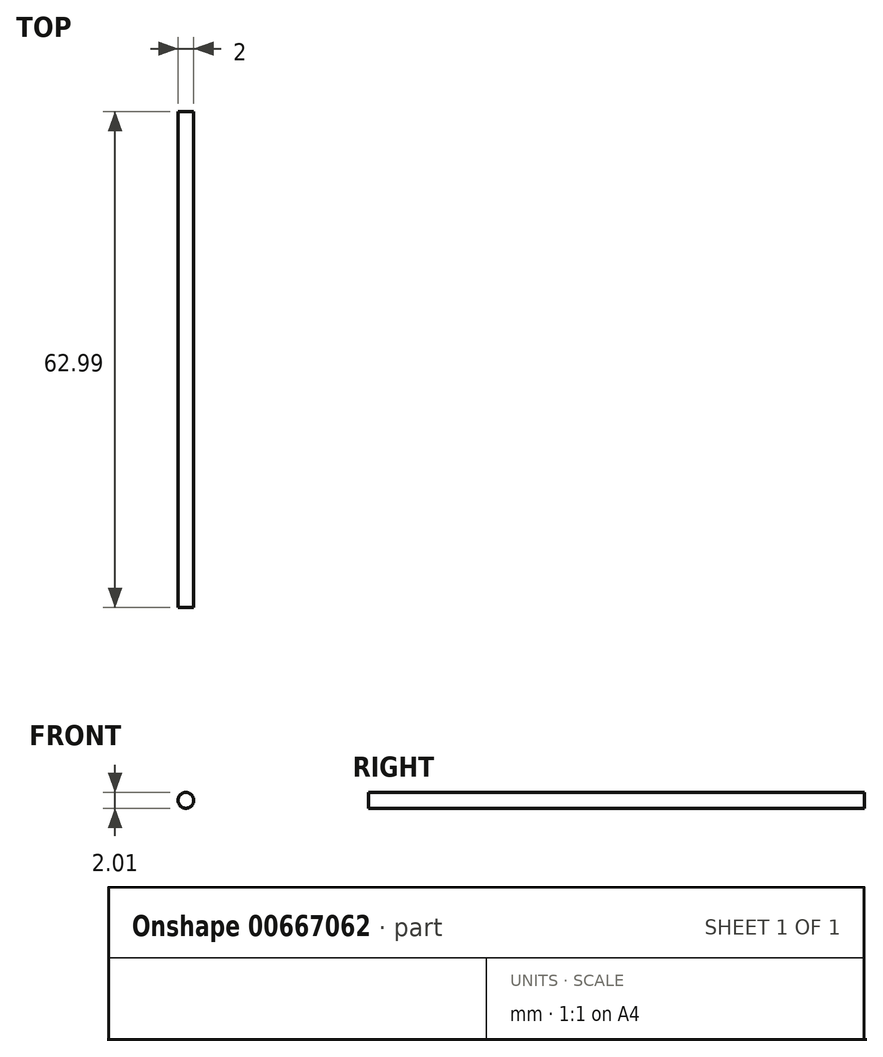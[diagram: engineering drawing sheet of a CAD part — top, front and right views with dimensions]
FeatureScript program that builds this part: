
annotation { "Feature Type Name" : "Feature", "Feature Type Description" : "" }
export const myFeature = defineFeature(function(context is Context, id is Id, definition is map)
    precondition{}
    {
        {
            var Q0;
            Q0=qCreatedBy(makeId("Front.planeOp"),FACE);
            var sketch = newSketch(context, id + "F0", { "sketchPlane" : qUnion([Q0])});
            skCircle(sketch, "E0", {"center": v(-42.49, 34.9) * mm, "radius": 1 * mm});
            skSolve(sketch);
        }
        {
            var Q0;
            Q0 = qSketchRegion(id + "F0", true);
            extrude(context, id + "F1", {"entities" : qUnion([Q0]), "oppositeDirection" : true, "depth" : 63 * mm, "offsetDistance" : 25.4 * mm});
        }
    });
